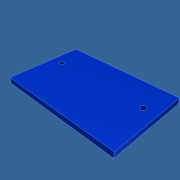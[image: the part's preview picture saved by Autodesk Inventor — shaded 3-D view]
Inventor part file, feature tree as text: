
AUTODESK INVENTOR PART (.ipt)
format: ipt  version: unknown  size: 166,400 bytes
history: native  units: mm
features: extrude x1, sketch x1
ambient origin geometry x8: Origin, YZ Plane, XZ Plane, XY Plane, X Axis, Y Axis, Z Axis, Center Point
feature tree (2):
  extrude  "Выдавливание1"  Depth=15.75mm
  sketch  "Эскиз1"
